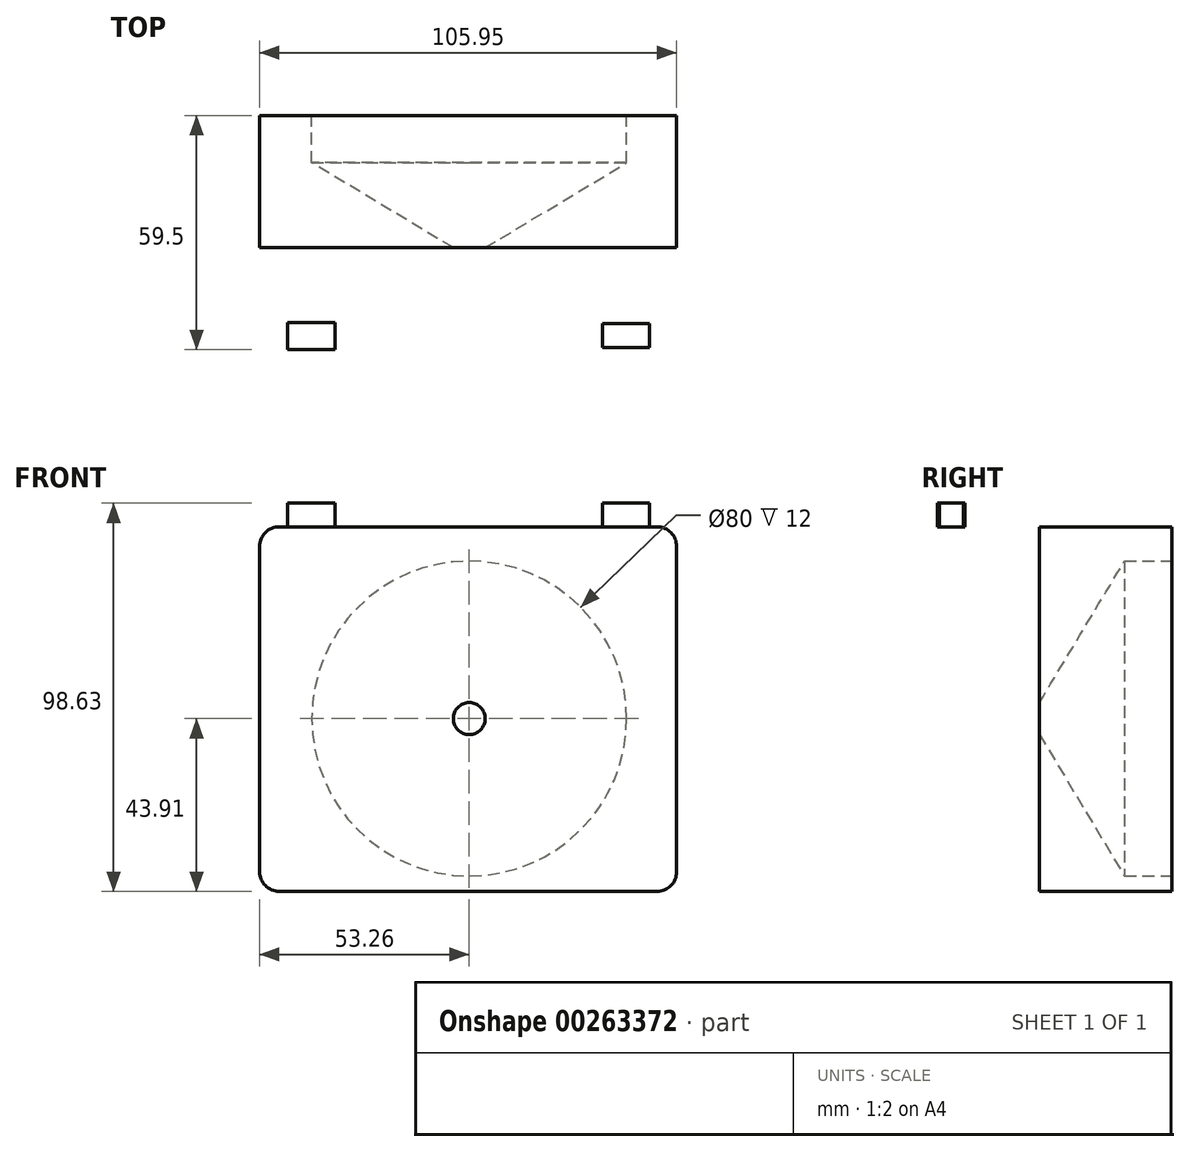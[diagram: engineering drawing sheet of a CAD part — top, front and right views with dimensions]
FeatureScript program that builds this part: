
annotation { "Feature Type Name" : "Feature", "Feature Type Description" : "" }
export const myFeature = defineFeature(function(context is Context, id is Id, definition is map)
    precondition{}
    {
        {
            var Q0;
            Q0=qCreatedBy(makeId("Front.planeOp"),FACE);
            var sketch = newSketch(context, id + "F0", { "sketchPlane" : qUnion([Q0])});
            skLineSegment(sketch, "E0.bottom", {"start": v(-53.26, 48.72) * mm, "end": v(52.69, 48.72) * mm});
            skLineSegment(sketch, "E0.top", {"start": v(-53.26, -43.9) * mm, "end": v(52.69, -43.9) * mm});
            skLineSegment(sketch, "E0.left", {"start": v(-53.26, 48.72) * mm, "end": v(-53.26, -43.9) * mm});
            skLineSegment(sketch, "E0.right", {"start": v(52.69, 48.72) * mm, "end": v(52.69, -43.9) * mm});
            skSolve(sketch);
        }
        {
            var Q0;
            Q0=makeQuery(id+"F0.imprint","IMPRINT",FACE,{"disambiguationData":[TD([[makeQuery(id+"F0.imprint","IMPRINT",EDGE,{"derivedFrom":sQuery(id+"F0.wireOp",EDGE,"E0.bottom")}),-1.0]])]});
            extrude(context, id + "F1", {"entities" : qUnion([Q0]), "oppositeDirection" : true, "depth" : 33.6 * mm});
        }
        {
            var Q0;
            Q0=makeQuery(id+"F1.opExtrude","CAP_FACE",FACE,{"disambiguationData":[OSD([sQuery(id+"F0.wireOp",EDGE,"E0.bottom"),sQuery(id+"F0.wireOp",EDGE,"E0.top"),sQuery(id+"F0.wireOp",EDGE,"E0.left"),sQuery(id+"F0.wireOp",EDGE,"E0.right")])],"isStart":false});
            var sketch = newSketch(context, id + "F2", { "sketchPlane" : qUnion([Q0])});
            skCircle(sketch, "E1", {"center": v(0, 0) * mm, "radius": 40.43 * mm});
            skSolve(sketch);
        }
        {
            var Q0;
            Q0=sQuery(id+"F2.wireOp",VERTEX,"E1.center");
            var Q1;
            Q1=makeQuery(id+"F1.opExtrude","SWEPT_BODY",BODY,{"disambiguationData":[OSD([sQuery(id+"F0.wireOp",EDGE,"E0.bottom"),sQuery(id+"F0.wireOp",EDGE,"E0.top"),sQuery(id+"F0.wireOp",EDGE,"E0.left"),sQuery(id+"F0.wireOp",EDGE,"E0.right")])]});
            hole(context, id + "F3", {"style" : HoleStyle.SIMPLE, "endStyle" : HoleEndStyle.BLIND, "holeDiameter" : 80 * mm, "holeDepth" : 12 * mm, "tappedDepth" : 12 * mm, "tapClearance" : 3, "locations" : qUnion([Q0]), "scope" : qUnion([Q1])});
        }
        {
            var Q0;
            Q0=makeQuery(id+"F1.opExtrude","SWEPT_EDGE",EDGE,{"disambiguationData":[OSD([sQuery(id+"F0.wireOp",EDGE,"E0.bottom"),sQuery(id+"F0.wireOp",EDGE,"E0.right")])]});
            var Q1;
            Q1=makeQuery(id+"F1.opExtrude","SWEPT_EDGE",EDGE,{"disambiguationData":[OSD([sQuery(id+"F0.wireOp",EDGE,"E0.bottom"),sQuery(id+"F0.wireOp",EDGE,"E0.left")])]});
            var Q2;
            Q2=makeQuery(id+"F1.opExtrude","SWEPT_EDGE",EDGE,{"disambiguationData":[OSD([sQuery(id+"F0.wireOp",EDGE,"E0.top"),sQuery(id+"F0.wireOp",EDGE,"E0.left")])]});
            var Q3;
            Q3=makeQuery(id+"F1.opExtrude","SWEPT_EDGE",EDGE,{"disambiguationData":[OSD([sQuery(id+"F0.wireOp",EDGE,"E0.top"),sQuery(id+"F0.wireOp",EDGE,"E0.right")])]});
            var Q4;
            Q4=makeQuery(id+"F3.hole-0.boolean.opBoolean","COPY",EDGE,{"derivedFrom":makeQuery(id+"F3.hole-0.opRevolve","SWEPT_EDGE",EDGE,{"disambiguationData":[OSD([sQuery(id+"F3.hole-0.sketch.wireOp",EDGE,"core_line_2"),sQuery(id+"F3.hole-0.sketch.wireOp",EDGE,"core_line_3")])]})});
            var Q5;
            {var subQ0=sQuery(id+"F0.wireOp",EDGE,"E0.right");var subQ1=sQuery(id+"F0.wireOp",EDGE,"E0.left");var subQ2=sQuery(id+"F0.wireOp",EDGE,"E0.top");var subQ3=sQuery(id+"F0.wireOp",EDGE,"E0.bottom");Q5=makeQuery(id+"F3.hole-0.boolean.opBoolean","COPY",FACE,{"disambiguationData":[TD([makeQuery(id+"FpqzGR9zJncTyu6_1.opShell","OFFSET_FACE",FACE,{"disambiguationData":[OSD([subQ3,subQ2,subQ1,subQ0]),TDD([makeQuery(id+"F1.opExtrude","CAP_FACE",FACE,{"disambiguationData":[OSD([subQ3,subQ2,subQ1,subQ0])],"isStart":true})])]})])],"derivedFrom":makeQuery(id+"F3.hole-0.opRevolve","SWEPT_FACE",FACE,{"disambiguationData":[OSD([sQuery(id+"F3.hole-0.sketch.wireOp",EDGE,"core_line_1")])]})});}
            fillet(context, id + "F4", {"entities" : qUnion([Q0, Q1, Q2, Q3, Q4, Q5]), "radius" : 5 * mm, "tangentPropagation" : true, "allowEdgeOverflow" : false});
        }
        {
            var Q0;
            Q0=makeQuery(id+"F1.opExtrude","SWEPT_FACE",FACE,{"disambiguationData":[OSD([sQuery(id+"F0.wireOp",EDGE,"E0.bottom")])]});
            var sketch = newSketch(context, id + "F5", { "sketchPlane" : qUnion([Q0])});
            skLineSegment(sketch, "E2.bottom", {"start": v(-46.12, -19) * mm, "end": v(-34.07, -19) * mm});
            skLineSegment(sketch, "E2.top", {"start": v(-46.12, -25.9) * mm, "end": v(-34.07, -25.9) * mm});
            skLineSegment(sketch, "E2.left", {"start": v(-46.12, -19) * mm, "end": v(-46.12, -25.9) * mm});
            skLineSegment(sketch, "E2.right", {"start": v(-34.07, -19) * mm, "end": v(-34.07, -25.9) * mm});
            skLineSegment(sketch, "E3.bottom", {"start": v(33.81, -19.3) * mm, "end": v(45.76, -19.3) * mm});
            skLineSegment(sketch, "E3.top", {"start": v(33.81, -25.38) * mm, "end": v(45.76, -25.38) * mm});
            skLineSegment(sketch, "E3.left", {"start": v(33.81, -19.3) * mm, "end": v(33.81, -25.38) * mm});
            skLineSegment(sketch, "E3.right", {"start": v(45.76, -19.3) * mm, "end": v(45.76, -25.38) * mm});
            skSolve(sketch);
        }
        {
            var Q0;
            Q0 = qSketchRegion(id + "F5", true);
            extrude(context, id + "F6", {"entities" : qUnion([Q0]), "operationType" : NewBodyOperationType.ADD, "depth" : 6 * mm});
        }
    });
